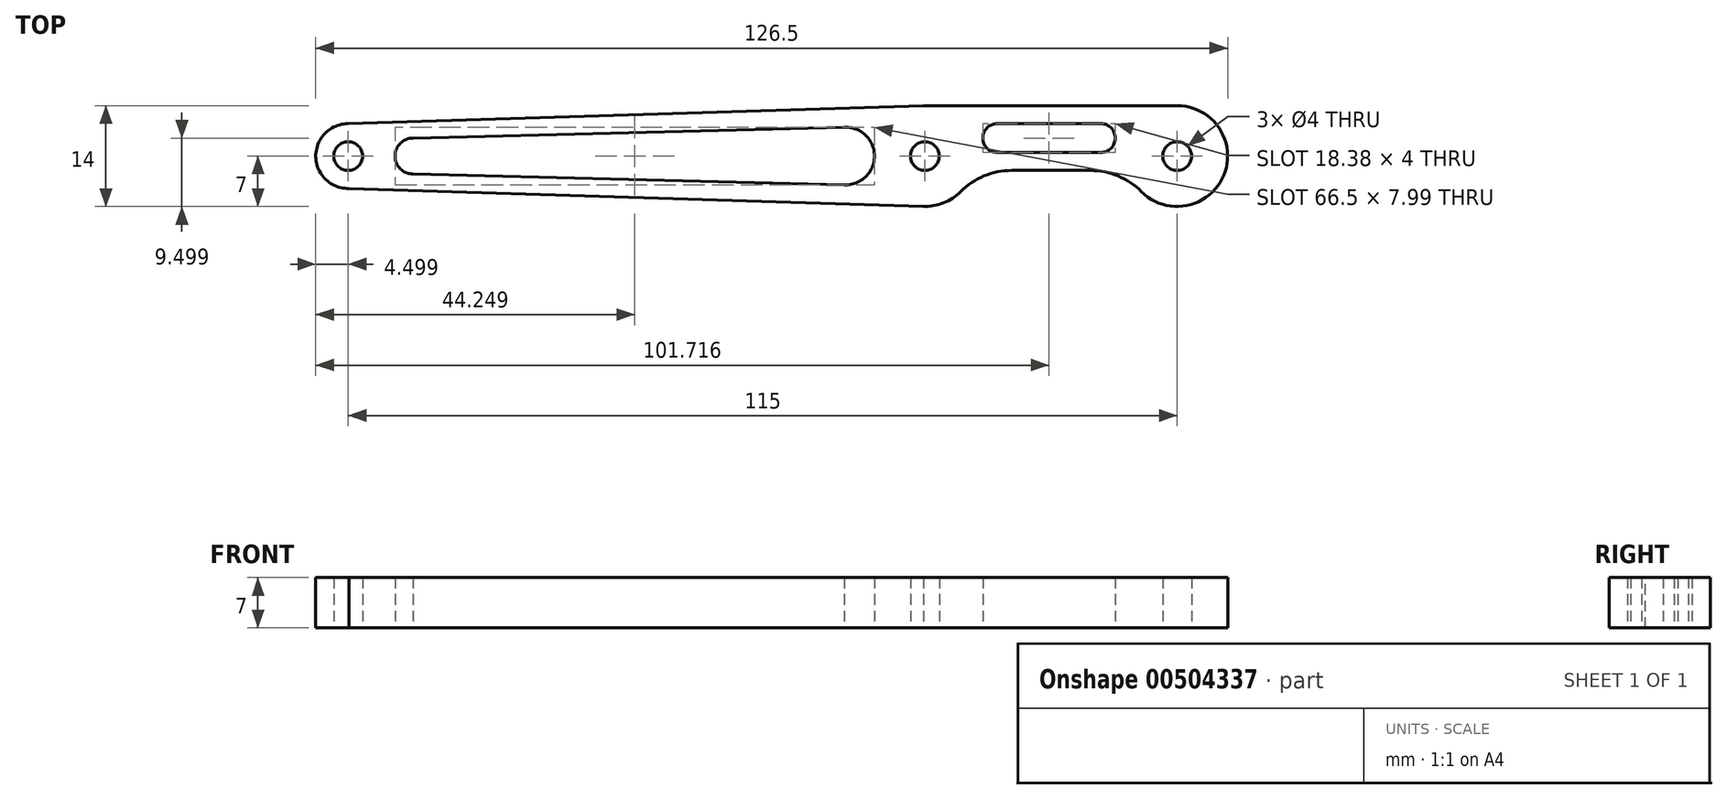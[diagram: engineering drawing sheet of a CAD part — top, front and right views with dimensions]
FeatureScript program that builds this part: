
annotation { "Feature Type Name" : "Feature", "Feature Type Description" : "" }
export const myFeature = defineFeature(function(context is Context, id is Id, definition is map)
    precondition{}
    {
        {
            var Q0;
            Q0=qCreatedBy(makeId("Top.planeOp"),FACE);
            var sketch = newSketch(context, id + "F0", { "sketchPlane" : qUnion([Q0])});
            skArc(sketch, "E0", {"start": v(-60.7, 14.27) * mm, "mid": v(-65.2, 9.7) * mm, "end": v(-60.56, 5.27) * mm});
            skArc(sketch, "E1", {"start": v(19.09, 2.77) * mm, "mid": v(23.4, 4.1) * mm, "end": v(26.02, 7.77) * mm});
            skArc(sketch, "E2", {"start": v(47.6, 7.77) * mm, "mid": v(59.92, 5.59) * mm, "end": v(54.3, 16.77) * mm});
            skCircle(sketch, "E3", {"center": v(-60.7, 9.77) * mm, "radius": 2 * mm});
            skCircle(sketch, "E4", {"center": v(19.3, 9.77) * mm, "radius": 2 * mm});
            skCircle(sketch, "E5", {"center": v(54.3, 9.77) * mm, "radius": 2 * mm});
            skLineSegment(sketch, "E6", {"start": v(-60.7, 14.27) * mm, "end": v(19.1, 16.77) * mm});
            skLineSegment(sketch, "E7", {"start": v(19.1, 16.77) * mm, "end": v(54.3, 16.77) * mm});
            skLineSegment(sketch, "E8", {"start": v(26.02, 7.77) * mm, "end": v(47.6, 7.77) * mm});
            skLineSegment(sketch, "E9", {"start": v(-60.56, 5.27) * mm, "end": v(19.09, 2.77) * mm});
            skArc(sketch, "E10.trimOffspring", {"start": v(19.53, 16.77) * mm, "mid": v(19.3, 16.77) * mm, "end": v(19.1, 16.77) * mm});
            skArc(sketch, "E11", {"start": v(-51.7, 12.27) * mm, "mid": v(-54.2, 9.77) * mm, "end": v(-51.7, 7.27) * mm});
            skArc(sketch, "E12", {"start": v(8.1, 5.77) * mm, "mid": v(12.3, 9.77) * mm, "end": v(8.1, 13.76) * mm});
            skLineSegment(sketch, "E13", {"start": v(-51.7, 7.27) * mm, "end": v(8.3, 5.77) * mm});
            skLineSegment(sketch, "E14", {"start": v(8.3, 13.77) * mm, "end": v(-51.7, 12.27) * mm});
            skArc(sketch, "E15", {"start": v(29.34, 14.27) * mm, "mid": v(27.34, 12.27) * mm, "end": v(29.34, 10.27) * mm});
            skArc(sketch, "E16", {"start": v(43.71, 10.27) * mm, "mid": v(45.71, 12.27) * mm, "end": v(43.71, 14.27) * mm});
            skLineSegment(sketch, "E17", {"start": v(29.34, 14.27) * mm, "end": v(43.71, 14.27) * mm});
            skLineSegment(sketch, "E18", {"start": v(29.34, 10.27) * mm, "end": v(43.71, 10.27) * mm});
            skPoint(sketch, "E19.orphan", {"position": v(37.8, 7.77) * mm});
            skPoint(sketch, "E20.start.orphan", {"position": v(37.8, 16.77) * mm});
            skSolve(sketch);
        }
        {
            var Q0;
            Q0=makeQuery(id+"F0.imprint","IMPRINT",FACE,{"disambiguationData":[TD([[makeQuery(id+"F0.imprint","IMPRINT",EDGE,{"derivedFrom":sQuery(id+"F0.wireOp",EDGE,"E0")}),1.0]])]});
            extrude(context, id + "F1", {"entities" : qUnion([Q0]), "depth" : 3.5 * mm, "hasSecondDirection" : true, "secondDirectionOppositeDirection" : true, "secondDirectionDepth" : 3.5 * mm});
        }
        {
            var Q0;
            Q0=makeQuery(id+"F1.opExtrude","SWEPT_EDGE",EDGE,{"disambiguationData":[OSD([sQuery(id+"F0.wireOp",EDGE,"E1"),sQuery(id+"F0.wireOp",EDGE,"E8")])]});
            var Q1;
            Q1=makeQuery(id+"F1.opExtrude","SWEPT_EDGE",EDGE,{"disambiguationData":[OSD([sQuery(id+"F0.wireOp",EDGE,"E2"),sQuery(id+"F0.wireOp",EDGE,"E8")])]});
            fillet(context, id + "F2", {"entities" : qUnion([Q0, Q1]), "radius" : 10 * mm, "tangentPropagation" : true, "allowEdgeOverflow" : false});
        }
    });
